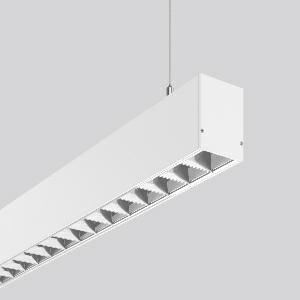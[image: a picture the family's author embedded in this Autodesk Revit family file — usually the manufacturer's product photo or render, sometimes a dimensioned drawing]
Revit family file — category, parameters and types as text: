
# Revit family: less_is_more_50_312344_002_273b
name_source: partatom
category: Lighting Fixtures
units: mm (PartAtom-declared; Revit-internal decimal feet)

## family parameters
Cut with Voids When Loaded = No
Host = Face
Light Source = No
Part Type = Normal
Room Calculation Point = No
Round Connector Dimension = Use Diameter
Shared = No

## types (1)
- LESS IS MORE 50 (1 x LED Modul 830, 7200 lm, 3000)
    Apparent Load = 64 VA
    CIE Flux Codes = 95 100 100 63 100
    Color Rendering = 80
    Color Temperature = 3000
    Default Elevation = 1800 mm
    Description = Series: LESS IS MORE 50
Linear pendant luminaire for aesthetically sophisticated lighting. Housing: extruded aluminium profile, powder-coated. End cap aluminium powder-coated. Canopy made of aluminium, powder-coated. Alea optical system: Reflector structure (ABS, Aluminium-coated, highly polished) with integrated diffuser made of non-yellowing plastic (PMMA) opal for glare-free light at the workstation (screen-compliant according to EN 12464-1). Direct 65%, indirect 35% light emission. Suitable for pendant. 2-point steel cable suspension freely positionable and infinitely height-adjustable. Special lengths available on request. LED unit with integrated converter interchangeable and removable. Suitable for through-wiring. With sensors or as a safety luminaire on request. 
Colour: traffic white, matt (RAL 9016)
Length: 1687 mm
Width: 57 mm
Height: 75 mm
Suspension length: 2000 mm
Lamp: LED
Socket: without socket
Colour temperature: 3000K
Colour rendering index (CRI): 80
Light source: LED
Socket lamp2: Without base
Colour temperature: 3000K
System power: 64 W
Rated luminous flux: 7200 lm
Luminous efficiency: 113 lm/W
Control gear: Regulated power supply
Control gear: Regulated power supply
Protection class: I
Type of protection: IP 20
    Height = 75 mm
    Lamp = 1 x LED Modul 830
    Lamp Light Flux = 7200 lm
    Lamp count = 1
    Length = 1687 mm
    Lifetime = 50000 h
    Luminous efficacy = 113 lm/W
    Manufacturer = RZB
    ModVariant = No
    Model = 312344.002
    Mounting Place = Ceiling
    Mounting Type = Pendant
    Number of Poles = 1
    OnlyDefault = Yes
    Power Factor = 1
    Product Name = LESS IS MORE 50
    Product group = Pendant LED linear luminaires
    ProductGroupID = 907
    Protection Class = Protection class I
    Protection Degree = IP 20
    RLX_Detail_Level = 1
    RLX_Emergency_Light_Flux = 0 lm
    RLX_Emergency_Type = 0
    RLX_Emergency_Type_DB = No
    RlxData = <blob elided: 37445 chars, md5=f216ba3a>
    Socket = socket
    Standby Power = 0 W
    System Light Flux = 7200 lm
    System Power = 64 W
    Type Comments = Product without accessories
    Type Image = 312342.002.jpg
    URL = http://relux.com
    VarID = ---
    Voltage = 230 V
    Voltage Range = 220-240 V
    Weight = 0.00 kg
    Width = 57 mm

## geometry (parser evidence)
native form markers: Blend x4, Sweep x11
no freeform markers — native parametric forms only
